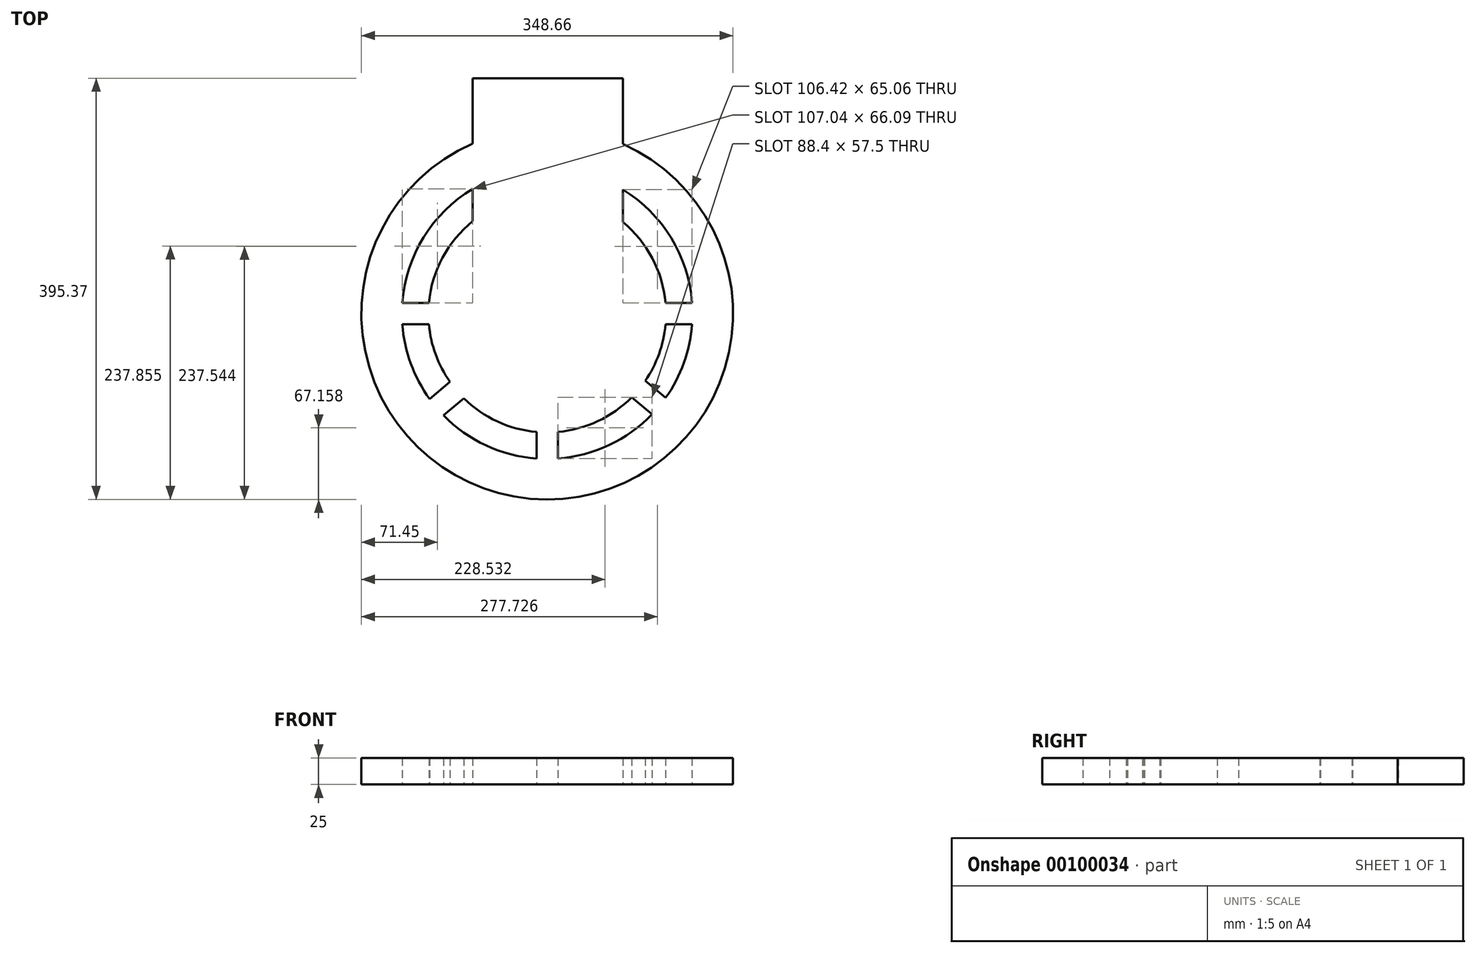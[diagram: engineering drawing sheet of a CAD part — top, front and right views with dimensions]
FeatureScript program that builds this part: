
annotation { "Feature Type Name" : "Feature", "Feature Type Description" : "" }
export const myFeature = defineFeature(function(context is Context, id is Id, definition is map)
    precondition{}
    {
        {
            var Q0;
            Q0=qCreatedBy(makeId("Top.planeOp"),FACE);
            var sketch = newSketch(context, id + "F0", { "sketchPlane" : qUnion([Q0])});
            skLineSegment(sketch, "E0", {"start": v(70.87, 93.93) * mm, "end": v(70.87, -186.07) * mm});
            skLineSegment(sketch, "E1", {"start": v(70.87, -186.07) * mm, "end": v(-69.83, -186.07) * mm});
            skLineSegment(sketch, "E2", {"start": v(-69.83, -186.07) * mm, "end": v(-69.83, 93.93) * mm});
            skLineSegment(sketch, "E3", {"start": v(-69.83, 93.93) * mm, "end": v(70.87, 93.93) * mm});
            skSolve(sketch);
        }
        {
            var Q0;
            Q0=makeQuery(id+"F0.imprint","IMPRINT",FACE,{"disambiguationData":[TD([[makeQuery(id+"F0.imprint","IMPRINT",EDGE,{"derivedFrom":sQuery(id+"F0.wireOp",EDGE,"E0")}),-1.0]])]});
            extrude(context, id + "F1", {"entities" : qUnion([Q0]), "depth" : 25 * mm});
        }
        {
            var Q0;
            Q0=qCreatedBy(makeId("Top.planeOp"),FACE);
            var sketch = newSketch(context, id + "F2", { "sketchPlane" : qUnion([Q0])});
            skCircle(sketch, "E4", {"center": v(0, -127.1) * mm, "radius": 136.3 * mm});
            skCircle(sketch, "E5", {"center": v(0, -127.1) * mm, "radius": 174.33 * mm});
            skCircle(sketch, "E6", {"center": v(0, -127.1) * mm, "radius": 111.46 * mm});
            skLineSegment(sketch, "E7", {"start": v(-10, -238.12) * mm, "end": v(-10, -263.03) * mm});
            skLineSegment(sketch, "E8", {"start": v(10, -263.03) * mm, "end": v(10, -238.12) * mm});
            skLineSegment(sketch, "E9", {"start": v(-135.93, -117.1) * mm, "end": v(-111, -117.1) * mm});
            skLineSegment(sketch, "E10", {"start": v(-135.93, -137.1) * mm, "end": v(-111, -137.1) * mm});
            skLineSegment(sketch, "E11", {"start": v(111, -117.1) * mm, "end": v(135.93, -117.1) * mm});
            skLineSegment(sketch, "E12", {"start": v(111, -137.1) * mm, "end": v(135.93, -137.1) * mm});
            skLineSegment(sketch, "E13", {"start": v(-91.23, -191.13) * mm, "end": v(-110.26, -207.22) * mm});
            skLineSegment(sketch, "E14", {"start": v(-78.32, -206.4) * mm, "end": v(-97.35, -222.5) * mm});
            skLineSegment(sketch, "E15", {"start": v(79.2, -205.53) * mm, "end": v(98.4, -221.4) * mm});
            skLineSegment(sketch, "E16", {"start": v(91.94, -190.12) * mm, "end": v(111.14, -205.99) * mm});
            skSolve(sketch);
        }
        {
            var Q0;
            Q0=makeQuery(id+"F2.imprint","IMPRINT",FACE,{"disambiguationData":[TD([[makeQuery(id+"F2.imprint","IMPRINT",EDGE,{"derivedFrom":sQuery(id+"F2.wireOp",EDGE,"E6")}),1.0]])]});
            var Q1;
            Q1=makeQuery(id+"F2.imprint","IMPRINT",FACE,{"disambiguationData":[TD([[makeQuery(id+"F2.imprint","IMPRINT",EDGE,{"derivedFrom":sQuery(id+"F2.wireOp",EDGE,"E4")}),-1.0]])]});
            var Q2;
            {var subQ0=sQuery(id+"F2.wireOp",EDGE,"E7");Q2=makeQuery(id+"F2.imprint","IMPRINT",FACE,{"disambiguationData":[TD([[makeQuery(id+"F2.imprint","IMPRINT",EDGE,{"derivedFrom":subQ0}),1.0]])]});}
            var Q3;
            {var subQ0=sQuery(id+"F2.wireOp",EDGE,"E9");Q3=makeQuery(id+"F2.imprint","IMPRINT",FACE,{"disambiguationData":[TD([[makeQuery(id+"F2.imprint","IMPRINT",EDGE,{"derivedFrom":subQ0}),-1.0]])]});}
            var Q4;
            {var subQ0=sQuery(id+"F2.wireOp",EDGE,"E13");Q4=makeQuery(id+"F2.imprint","IMPRINT",FACE,{"disambiguationData":[TD([[makeQuery(id+"F2.imprint","IMPRINT",EDGE,{"derivedFrom":subQ0}),1.0]])]});}
            var Q5;
            {var subQ0=sQuery(id+"F2.wireOp",EDGE,"E15");Q5=makeQuery(id+"F2.imprint","IMPRINT",FACE,{"disambiguationData":[TD([[makeQuery(id+"F2.imprint","IMPRINT",EDGE,{"derivedFrom":subQ0}),1.0]])]});}
            var Q6;
            {var subQ0=sQuery(id+"F2.wireOp",EDGE,"E11");Q6=makeQuery(id+"F2.imprint","IMPRINT",FACE,{"disambiguationData":[TD([[makeQuery(id+"F2.imprint","IMPRINT",EDGE,{"derivedFrom":subQ0}),-1.0]])]});}
            extrude(context, id + "F3", {"entities" : qUnion([Q0, Q1, Q2, Q3, Q4, Q5, Q6]), "operationType" : NewBodyOperationType.ADD, "depth" : 25 * mm});
        }
    });
